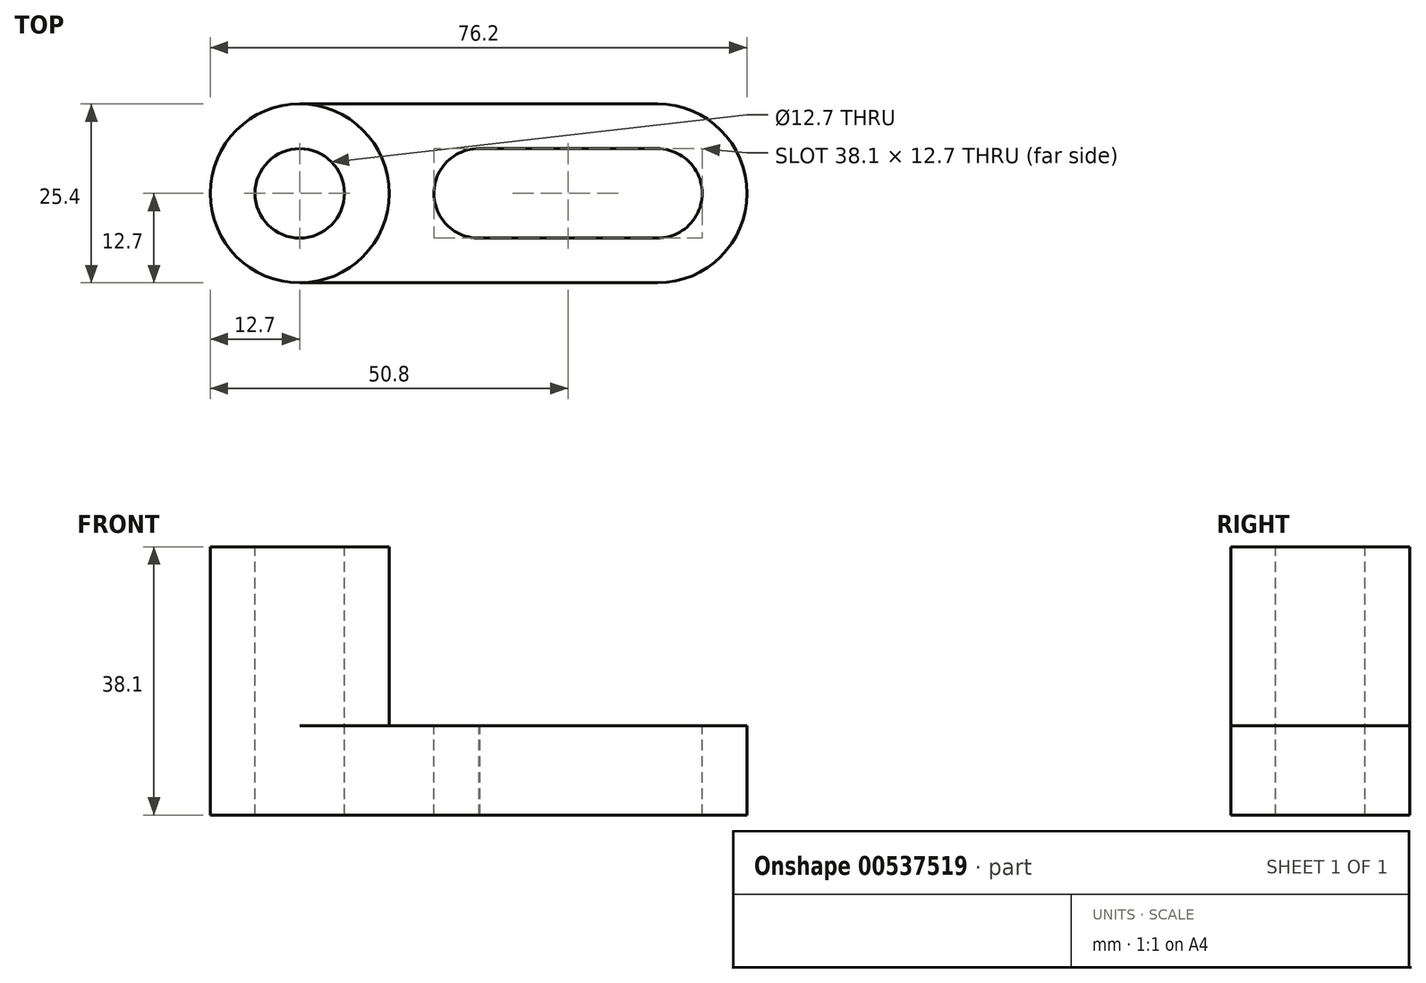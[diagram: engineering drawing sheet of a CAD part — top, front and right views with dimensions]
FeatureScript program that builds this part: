
annotation { "Feature Type Name" : "Feature", "Feature Type Description" : "" }
export const myFeature = defineFeature(function(context is Context, id is Id, definition is map)
    precondition{}
    {
        {
            var Q0;
            Q0=qCreatedBy(makeId("Front.planeOp"),FACE);
            var sketch = newSketch(context, id + "F0", { "sketchPlane" : qUnion([Q0])});
            skLineSegment(sketch, "E0", {"start": v(0, 0) * mm, "end": v(76.2, 0) * mm});
            skLineSegment(sketch, "E1", {"start": v(76.2, 0) * mm, "end": v(76.2, 38.1) * mm});
            skLineSegment(sketch, "E2", {"start": v(76.2, 38.1) * mm, "end": v(0, 38.1) * mm});
            skLineSegment(sketch, "E3", {"start": v(0, 38.1) * mm, "end": v(0, 0) * mm});
            skSolve(sketch);
        }
        {
            var Q0;
            Q0 = qSketchRegion(id + "F0", true);
            extrude(context, id + "F1", {"entities" : qUnion([Q0]), "depth" : 25.4 * mm, "offsetDistance" : 25.4 * mm});
        }
        {
            var Q0;
            Q0=makeQuery(id+"F1.opExtrude","CAP_FACE",FACE,{"disambiguationData":[OSD([sQuery(id+"F0.wireOp",EDGE,"E0"),sQuery(id+"F0.wireOp",EDGE,"E1"),sQuery(id+"F0.wireOp",EDGE,"E2"),sQuery(id+"F0.wireOp",EDGE,"E3")])],"isStart":false});
            var sketch = newSketch(context, id + "F2", { "sketchPlane" : qUnion([Q0])});
            skLineSegment(sketch, "E4", {"start": v(0, 38.1) * mm, "end": v(25.4, 38.1) * mm});
            skLineSegment(sketch, "E5", {"start": v(25.4, 38.1) * mm, "end": v(25.4, 12.7) * mm});
            skLineSegment(sketch, "E6", {"start": v(25.4, 12.7) * mm, "end": v(76.2, 12.7) * mm});
            skLineSegment(sketch, "E7", {"start": v(76.2, 12.7) * mm, "end": v(76.2, 0) * mm});
            skSolve(sketch);
        }
        {
            var Q0;
            Q0 = qSketchRegion(id + "F2", true);
            var Q1;
            {var subQ0=sQuery(id+"F2.wireOp",EDGE,"E5");Q1=makeQuery(id+"F2.imprint","IMPRINT",FACE,{"disambiguationData":[TD([[makeQuery(id+"F2.imprint","IMPRINT",EDGE,{"derivedFrom":subQ0}),1.0]])]});}
            extrude(context, id + "F3", {"entities" : qUnion([Q0, Q1]), "operationType" : NewBodyOperationType.REMOVE, "oppositeDirection" : true, "depth" : 25.4 * mm, "offsetDistance" : 25.4 * mm});
        }
        {
            var Q0;
            Q0=makeQuery(id+"F1.opExtrude","SWEPT_FACE",FACE,{"disambiguationData":[OSD([sQuery(id+"F0.wireOp",EDGE,"E2")])]});
            var sketch = newSketch(context, id + "F4", { "sketchPlane" : qUnion([Q0])});
            skCircle(sketch, "E8", {"center": v(12.7, -12.7) * mm, "radius": 12.7 * mm});
            skPoint(sketch, "E8.centerSnap0", {"position": v(0, -12.7) * mm});
            skPoint(sketch, "E8.centerSnap1", {"position": v(12.7, -25.4) * mm});
            skCircle(sketch, "E9", {"center": v(12.7, -12.7) * mm, "radius": 6.35 * mm});
            skSolve(sketch);
        }
        {
            var Q0;
            Q0=makeQuery(id+"F4.imprint","IMPRINT",FACE,{"disambiguationData":[TD([[makeQuery(id+"F4.imprint","IMPRINT",EDGE,{"derivedFrom":sQuery(id+"F4.wireOp",EDGE,"E9")}),1.0]])]});
            var Q1;
            {var subQ0=sQuery(id+"F4.wireOp",EDGE,"E8");var subQ1=sQuery(id+"F0.wireOp",EDGE,"E2");var subQ4=makeQuery(id+"F1.opExtrude","CAP_EDGE",EDGE,{"disambiguationData":[OSD([subQ1])],"isStart":false});var subQ5=makeQuery(id+"F4.imprint","INTERSECT",VERTEX,{"derivedFrom":[subQ4,subQ0]});Q1=makeQuery(id+"F4.imprint","IMPRINT",FACE,{"disambiguationData":[TD([[makeQuery(id+"F4.imprint","IMPRINT",EDGE,{"disambiguationData":[TD([[subQ5,1.0]])],"derivedFrom":subQ0}),-1.0]])]});}
            var Q2;
            {var subQ0=sQuery(id+"F4.wireOp",EDGE,"E8");var subQ1=sQuery(id+"F0.wireOp",EDGE,"E2");var subQ2=makeQuery(id+"F1.opExtrude","CAP_EDGE",EDGE,{"disambiguationData":[OSD([subQ1])],"isStart":true});var subQ3=makeQuery(id+"F4.imprint","INTERSECT",VERTEX,{"derivedFrom":[subQ2,subQ0]});Q2=makeQuery(id+"F4.imprint","IMPRINT",FACE,{"disambiguationData":[TD([[makeQuery(id+"F4.imprint","IMPRINT",EDGE,{"disambiguationData":[TD([[subQ3,-1.0]])],"derivedFrom":subQ0}),-1.0]])]});}
            extrude(context, id + "F5", {"entities" : qUnion([Q0, Q1, Q2]), "operationType" : NewBodyOperationType.REMOVE, "oppositeDirection" : true, "depth" : 38.1 * mm, "offsetDistance" : 25.4 * mm});
        }
        {
            var Q0;
            Q0 = qSketchRegion(id + "F4", true);
            var Q1;
            Q1=makeQuery(id+"F1.opExtrude","SWEPT_FACE",FACE,{"disambiguationData":[OSD([sQuery(id+"F0.wireOp",EDGE,"E2")])]});
            extrude(context, id + "F6", {"entities" : qUnion([Q0, Q1]), "operationType" : NewBodyOperationType.REMOVE, "oppositeDirection" : true, "depth" : 25.4 * mm, "offsetDistance" : 25.4 * mm});
        }
        {
            var Q0;
            Q0 = qSketchRegion(id + "F4", true);
            extrude(context, id + "F7", {"entities" : qUnion([Q0]), "operationType" : NewBodyOperationType.ADD, "oppositeDirection" : true, "depth" : 25.4 * mm, "offsetDistance" : 25.4 * mm});
        }
        {
            var Q0;
            Q0=makeQuery(id+"F6.boolean.opBoolean","MERGE",FACE,{"derivedFrom":[makeQuery(id+"F3.boolean.opBoolean","COPY",FACE,{"derivedFrom":makeQuery(id+"F3.opExtrude","SWEPT_FACE",FACE,{"disambiguationData":[OSD([sQuery(id+"F2.wireOp",EDGE,"E6")])]})}),makeQuery(id+"F6.opExtrude","CAP_FACE",FACE,{"disambiguationData":[OSD([sQuery(id+"F4.wireOp",EDGE,"E8"),sQuery(id+"F4.wireOp",EDGE,"E9")])],"isStart":false}),makeQuery(id+"F6.opExtrude","CAP_FACE",FACE,{"disambiguationData":[OSD([sQuery(id+"F0.wireOp",EDGE,"E2")])],"isStart":false})]});
            var sketch = newSketch(context, id + "F8", { "sketchPlane" : qUnion([Q0])});
            skCircle(sketch, "E10", {"center": v(38.1, -12.7) * mm, "radius": 6.35 * mm});
            skPoint(sketch, "E10.centerSnap0", {"position": v(76.2, -12.7) * mm});
            skCircle(sketch, "E11", {"center": v(63.5, -12.7) * mm, "radius": 6.35 * mm});
            skLineSegment(sketch, "E12", {"start": v(38.01, -6.35) * mm, "end": v(63.5, -6.35) * mm});
            skLineSegment(sketch, "E13", {"start": v(38.31, -19.05) * mm, "end": v(63.5, -19.05) * mm});
            skArc(sketch, "E14", {"start": v(63.5, -25.4) * mm, "mid": v(76.2, -12.7) * mm, "end": v(63.5, 0) * mm});
            skSolve(sketch);
        }
        {
            var Q0;
            {var subQ0=sQuery(id+"F8.wireOp",EDGE,"E12");var subQ1=sQuery(id+"F8.wireOp",EDGE,"E10");var subQ2=makeQuery(id+"F8.imprint","INTERSECT",VERTEX,{"disambiguationData":[OD(0.0)],"derivedFrom":[subQ1,subQ0]});Q0=makeQuery(id+"F8.imprint","IMPRINT",FACE,{"disambiguationData":[TD([[makeQuery(id+"F8.imprint","IMPRINT",EDGE,{"disambiguationData":[TD([[subQ2,1.0]])],"derivedFrom":subQ1}),1.0]])]});}
            var Q1;
            {var subQ0=sQuery(id+"F8.wireOp",EDGE,"E11");var subQ1=makeQuery(id+"F8.imprint","INTERSECT",VERTEX,{"derivedFrom":[subQ0,sQuery(id+"F8.wireOp",EDGE,"E12")]});Q1=makeQuery(id+"F8.imprint","IMPRINT",FACE,{"disambiguationData":[TD([[makeQuery(id+"F8.imprint","IMPRINT",EDGE,{"disambiguationData":[TD([[subQ1,-1.0]])],"derivedFrom":subQ0}),1.0]])]});}
            var Q2;
            {var subQ0=sQuery(id+"F8.wireOp",EDGE,"E12");var subQ1=sQuery(id+"F8.wireOp",EDGE,"E10");var subQ2=makeQuery(id+"F8.imprint","INTERSECT",VERTEX,{"disambiguationData":[OD(0.0)],"derivedFrom":[subQ1,subQ0]});Q2=makeQuery(id+"F8.imprint","IMPRINT",FACE,{"disambiguationData":[TD([[makeQuery(id+"F8.imprint","IMPRINT",EDGE,{"disambiguationData":[TD([[subQ2,-1.0]])],"derivedFrom":subQ1}),1.0]])]});}
            var Q3;
            {var subQ0=sQuery(id+"F8.wireOp",EDGE,"E13");Q3=makeQuery(id+"F8.imprint","IMPRINT",FACE,{"disambiguationData":[TD([[makeQuery(id+"F8.imprint","IMPRINT",EDGE,{"derivedFrom":subQ0}),1.0]])]});}
            var Q4;
            {var subQ0=sQuery(id+"F8.wireOp",EDGE,"E14");var subQ1=sQuery(id+"F0.wireOp",EDGE,"E2");var subQ2=sQuery(id+"F2.wireOp",EDGE,"E6");var subQ3=makeQuery(id+"F6.boolean.opBoolean","MERGE",EDGE,{"derivedFrom":[makeQuery(id+"F3.boolean.opBoolean","COPY",EDGE,{"derivedFrom":makeQuery(id+"F3.opExtrude","CAP_EDGE",EDGE,{"disambiguationData":[OSD([subQ2])],"isStart":false})}),makeQuery(id+"F6.opExtrude","CAP_EDGE",EDGE,{"disambiguationData":[OSD([subQ1]),TDD([makeQuery(id+"F1.opExtrude","CAP_EDGE",EDGE,{"disambiguationData":[OSD([subQ1])],"isStart":true})])],"isStart":false})]});var subQ4=makeQuery(id+"F8.imprint","INTERSECT",VERTEX,{"derivedFrom":[subQ3,subQ0]});Q4=makeQuery(id+"F8.imprint","IMPRINT",FACE,{"disambiguationData":[TD([[makeQuery(id+"F8.imprint","IMPRINT",EDGE,{"disambiguationData":[TD([[subQ4,1.0]])],"derivedFrom":subQ0}),-1.0]])]});}
            var Q5;
            {var subQ0=sQuery(id+"F8.wireOp",EDGE,"E14");var subQ1=sQuery(id+"F0.wireOp",EDGE,"E2");var subQ2=sQuery(id+"F2.wireOp",EDGE,"E6");var subQ3=makeQuery(id+"F6.boolean.opBoolean","MERGE",EDGE,{"derivedFrom":[makeQuery(id+"F3.boolean.opBoolean","COPY",EDGE,{"derivedFrom":makeQuery(id+"F3.opExtrude","CAP_EDGE",EDGE,{"disambiguationData":[OSD([subQ2])],"isStart":true})}),makeQuery(id+"F6.opExtrude","CAP_EDGE",EDGE,{"disambiguationData":[OSD([subQ1]),TDD([makeQuery(id+"F1.opExtrude","CAP_EDGE",EDGE,{"disambiguationData":[OSD([subQ1])],"isStart":false})])],"isStart":false})]});var subQ4=makeQuery(id+"F8.imprint","INTERSECT",VERTEX,{"derivedFrom":[subQ3,subQ0]});Q5=makeQuery(id+"F8.imprint","IMPRINT",FACE,{"disambiguationData":[TD([[makeQuery(id+"F8.imprint","IMPRINT",EDGE,{"disambiguationData":[TD([[subQ4,-1.0]])],"derivedFrom":subQ0}),-1.0]])]});}
            extrude(context, id + "F9", {"entities" : qUnion([Q0, Q1, Q2, Q3, Q4, Q5]), "operationType" : NewBodyOperationType.REMOVE, "oppositeDirection" : true, "depth" : 12.7 * mm, "offsetDistance" : 25.4 * mm});
        }
    });
